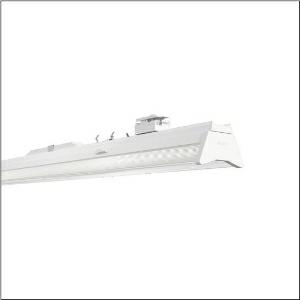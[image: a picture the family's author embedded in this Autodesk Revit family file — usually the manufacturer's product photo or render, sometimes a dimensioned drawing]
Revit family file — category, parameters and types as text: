
# Revit family: licross_r__21_performance_ho_52tm16cn4c5m_51b1
name_source: partatom
category: Lighting Fixtures
units: mm (PartAtom-declared; Revit-internal decimal feet)

## family parameters
Cut with Voids When Loaded = No
Host = Face
Light Source = No
Part Type = Normal
Room Calculation Point = No
Round Connector Dimension = Use Diameter
Shared = No

## types (1)
- --- (1 x LED, 12610 lm, 68.9 W, 4000K)
    Apparent Load = 69 VA
    CIE Flux Codes = 63 87 95 78 100
    Color Rendering = 80
    Color Temperature = 4000K
    Default Elevation = 1800 mm
    Description = Licross® 21 Performance HO, luminaire insert, of sheet steel, galvanised, coil coated, white, length: 1.500mm, width: 120mm, height: 123mm, LED rated luminous flux: 12.610lm, light colour: 840, control gear: ON/OFF Multilumen, CLOi, control gear: ECG Multilumen, with plug, 3-pole, with phase selection, mains connection: 220..240V, AC, 50/60Hz, start of lifetime: 69W, end of service life: 83W, internal wiring halogen-free, primary light control with lens, of plastic, primary optical cover: cover, of PMMA, light emission: direct/indirect distribution, primary light characteristic: symmetric, protection rating (complete): IP40, insulation class (complete): insulation class I (protective earthing), certification: CE, ENEC, UKCA, protection symbol: D if used in an environment without relevant dust loads with corresponding accessories, impact resistance: IK06, permissible ambient temperature for indoor applications: -35..+35°C, corresponds to IFS (International Featured Standards) requirements for safety and quality in the food industry, reducing of maximum allowable ambient temperature of 5°C with ceiling mounting, LABS conformity tested according to VDMA 24364:2018-05, packaging unit: 1 piece
    Height = 114 mm
    Lamp = 1 x LED
    Lamp Light Flux = 12610 lm
    Lamp Power = 68.9 W
    Lamp count = 1
    Length = 1500 mm
    Luminous efficacy = 183 lm/W
    Manufacturer = Siteco
    ModVariant = No
    Model = 52TM16CN4C5M
    Mounting Place = Ceiling
    Mounting Type = Pendant
    Number of Poles = 1
    OnlyDefault = Yes
    Power Factor = 1
    Product Name = Licross® 21 Performance HO
    Product group = luminaire insert | ceiling pendant
    ProductGroupID = 902
    Protection Class = Protection class I
    Protection Degree = IP 40
    RLX_Detail_Level = 1
    RLX_Emergency_Light_Flux = 0 lm
    RLX_Emergency_Type = 0
    RLX_Emergency_Type_DB = No
    RlxData = <blob elided: 31821 chars, md5=87aef6c6>
    Socket = socket
    Standby Power = 0 W
    System Light Flux = 12610 lm
    System Power = 69 W
    Type Comments = factory setting: luminous flux: 100 % | (A | C | E) | 162 mA
    Type Image = l_1256138.jpg
    URL = http://relux.com
    VarID = @adj_133107
    Voltage = 0 V
    Weight = 0.00 kg
    Width = 120 mm

## geometry (parser evidence)
native form markers: Blend x4, Sweep x12
no freeform markers — native parametric forms only
